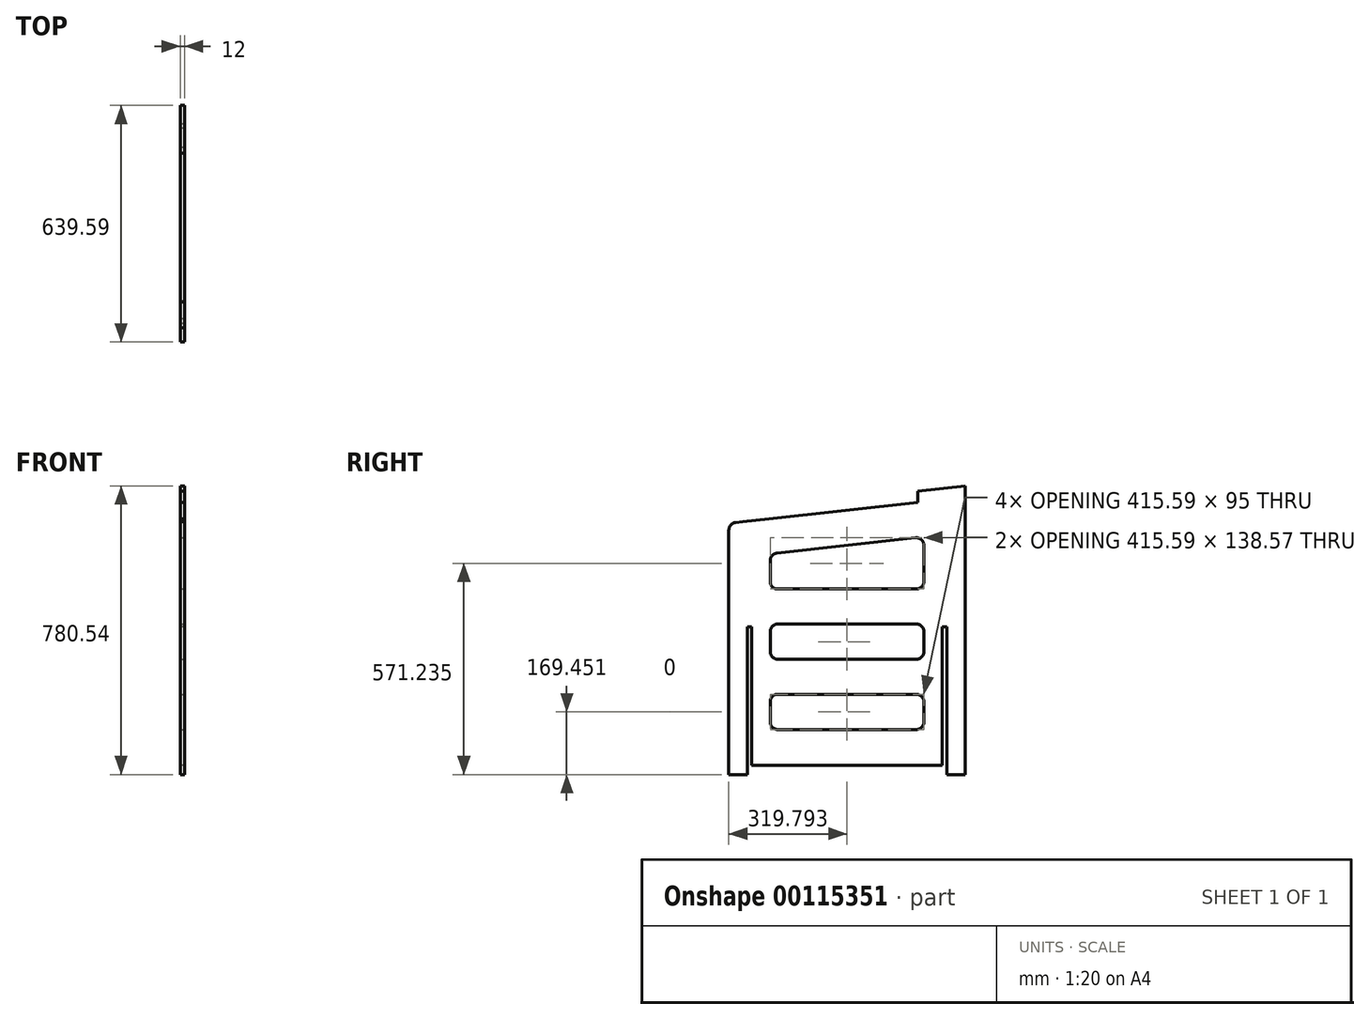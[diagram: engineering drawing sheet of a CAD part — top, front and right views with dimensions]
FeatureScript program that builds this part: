
annotation { "Feature Type Name" : "Feature", "Feature Type Description" : "" }
export const myFeature = defineFeature(function(context is Context, id is Id, definition is map)
    precondition{}
    {
        {
            var Q0;
            Q0=qCreatedBy(makeId("Right.planeOp"),FACE);
            var sketch = newSketch(context, id + "F0", { "sketchPlane" : qUnion([Q0])});
            skLineSegment(sketch, "E0.bottom", {"start": v(-516.8, 134.02) * mm, "end": v(183.2, 127.7) * mm, "construction": true});
            skLineSegment(sketch, "E0.left", {"start": v(-516.8, 134.02) * mm, "end": v(-516.8, 50.2) * mm, "construction": true});
            skLineSegment(sketch, "E1", {"start": v(60.78, -259.53) * mm, "end": v(72.78, -259.53) * mm});
            skLineSegment(sketch, "E2", {"start": v(-466.8, -259.53) * mm, "end": v(-454.8, -259.53) * mm});
            skLineSegment(sketch, "E3", {"start": v(-454.8, -634.53) * mm, "end": v(60.78, -634.53) * mm});
            skLineSegment(sketch, "E4", {"start": v(-478.83, 54.41) * mm, "end": v(-478.83, 24.23) * mm});
            skLineSegment(sketch, "E5", {"start": v(-478.83, 24.23) * mm, "end": v(-498.92, 22.1) * mm});
            skLineSegment(sketch, "E6", {"start": v(-516.8, 2.21) * mm, "end": v(-516.8, -659.53) * mm});
            skLineSegment(sketch, "E7", {"start": v(-516.8, 50.2) * mm, "end": v(-516.8, 20.2) * mm, "construction": true});
            skLineSegment(sketch, "E8", {"start": v(-408.83, 31.98) * mm, "end": v(-5.76, 76.6) * mm});
            skLineSegment(sketch, "E9", {"start": v(-408.83, 62.16) * mm, "end": v(-408.83, 31.98) * mm});
            skLineSegment(sketch, "E10", {"start": v(-516.8, -659.53) * mm, "end": v(-466.8, -659.53) * mm});
            skLineSegment(sketch, "E11", {"start": v(-466.8, -259.53) * mm, "end": v(-466.8, -659.53) * mm});
            skLineSegment(sketch, "E12", {"start": v(-454.8, -259.53) * mm, "end": v(-454.8, -634.53) * mm});
            skLineSegment(sketch, "E13", {"start": v(60.78, -259.53) * mm, "end": v(60.78, -634.53) * mm});
            skLineSegment(sketch, "E14", {"start": v(72.78, -259.53) * mm, "end": v(72.78, -659.53) * mm});
            skLineSegment(sketch, "E15", {"start": v(-516.8, 50.2) * mm, "end": v(-478.83, 54.41) * mm, "construction": true});
            skLineSegment(sketch, "E16", {"start": v(-5.76, 76.6) * mm, "end": v(-5.76, 106.78) * mm});
            skLineSegment(sketch, "E17", {"start": v(-478.83, 54.41) * mm, "end": v(-408.83, 62.16) * mm});
            skLineSegment(sketch, "E18", {"start": v(-408.83, 62.16) * mm, "end": v(-5.76, 106.78) * mm, "construction": true});
            skLineSegment(sketch, "E19", {"start": v(-5.76, 106.78) * mm, "end": v(122.78, 121) * mm});
            skLineSegment(sketch, "E20", {"start": v(122.78, 121) * mm, "end": v(183.2, 127.7) * mm, "construction": true});
            skLineSegment(sketch, "E21", {"start": v(122.78, 121) * mm, "end": v(122.78, -659.53) * mm});
            skLineSegment(sketch, "E22", {"start": v(72.78, -259.53) * mm, "end": v(72.78, 115.47) * mm, "construction": true});
            skLineSegment(sketch, "E23", {"start": v(72.78, -659.53) * mm, "end": v(122.78, -659.53) * mm});
            skLineSegment(sketch, "E24", {"start": v(183.2, 127.7) * mm, "end": v(183.2, -659.53) * mm, "construction": true});
            skLineSegment(sketch, "E25", {"start": v(122.78, -659.53) * mm, "end": v(183.2, -659.53) * mm, "construction": true});
            skPoint(sketch, "E26.visualSharp", {"position": v(-516.8, 20.2) * mm});
            skArc(sketch, "E26.filletArc", {"start": v(-498.92, 22.1) * mm, "mid": v(-511.68, 15.59) * mm, "end": v(-516.8, 2.21) * mm});
            skSolve(sketch);
        }
        {
            var Q0;
            Q0=makeQuery(id+"F0.imprint","IMPRINT",FACE,{"disambiguationData":[TD([[makeQuery(id+"F0.imprint","IMPRINT",EDGE,{"derivedFrom":sQuery(id+"F0.wireOp",EDGE,"E1")}),1.0]])]});
            extrude(context, id + "F1", {"entities" : qUnion([Q0]), "depth" : 12 * mm});
        }
        {
            var Q0;
            Q0=makeQuery(id+"F1.opExtrude","CAP_FACE",FACE,{"disambiguationData":[OSD([sQuery(id+"F0.wireOp",EDGE,"E1"),sQuery(id+"F0.wireOp",EDGE,"E2"),sQuery(id+"F0.wireOp",EDGE,"E3"),sQuery(id+"F0.wireOp",EDGE,"E4"),sQuery(id+"F0.wireOp",EDGE,"E5"),sQuery(id+"F0.wireOp",EDGE,"E6"),sQuery(id+"F0.wireOp",EDGE,"E8"),sQuery(id+"F0.wireOp",EDGE,"E9"),sQuery(id+"F0.wireOp",EDGE,"E10"),sQuery(id+"F0.wireOp",EDGE,"E11"),sQuery(id+"F0.wireOp",EDGE,"E12"),sQuery(id+"F0.wireOp",EDGE,"E13"),sQuery(id+"F0.wireOp",EDGE,"E14"),sQuery(id+"F0.wireOp",EDGE,"E16"),sQuery(id+"F0.wireOp",EDGE,"E17"),sQuery(id+"F0.wireOp",EDGE,"E19"),sQuery(id+"F0.wireOp",EDGE,"E21"),sQuery(id+"F0.wireOp",EDGE,"E23"),sQuery(id+"F0.wireOp",EDGE,"E26.filletArc")])],"isStart":false});
            var sketch = newSketch(context, id + "F2", { "sketchPlane" : qUnion([Q0])});
            skLineSegment(sketch, "E27.left", {"start": v(-404.8, -462.58) * mm, "end": v(-404.8, -517.58) * mm});
            skLineSegment(sketch, "E28.left", {"start": v(-404.8, -272.58) * mm, "end": v(-404.8, -327.58) * mm});
            skLineSegment(sketch, "E29.left", {"start": v(-404.8, -80.49) * mm, "end": v(-404.8, -137.58) * mm});
            skPoint(sketch, "E30", {"position": v(-404.8, -634.53) * mm});
            skPoint(sketch, "E31", {"position": v(-404.8, 32.42) * mm});
            skLineSegment(sketch, "E32", {"start": v(-387.01, -60.6) * mm, "end": v(-11.42, -19.03) * mm});
            skLineSegment(sketch, "E33", {"start": v(10.78, -38.91) * mm, "end": v(10.78, -137.58) * mm});
            skLineSegment(sketch, "E34", {"start": v(-9.22, -157.58) * mm, "end": v(-384.8, -157.58) * mm});
            skLineSegment(sketch, "E35", {"start": v(-384.8, -252.58) * mm, "end": v(-9.22, -252.58) * mm});
            skLineSegment(sketch, "E36", {"start": v(10.78, -272.58) * mm, "end": v(10.78, -327.58) * mm});
            skLineSegment(sketch, "E37", {"start": v(-9.22, -347.58) * mm, "end": v(-384.8, -347.58) * mm});
            skLineSegment(sketch, "E38", {"start": v(-384.8, -442.58) * mm, "end": v(-9.22, -442.58) * mm});
            skLineSegment(sketch, "E39", {"start": v(10.78, -462.58) * mm, "end": v(10.78, -517.58) * mm});
            skLineSegment(sketch, "E40", {"start": v(-9.22, -537.58) * mm, "end": v(-384.8, -537.58) * mm});
            skPoint(sketch, "E41.visualSharp", {"position": v(-404.8, -62.58) * mm});
            skArc(sketch, "E41.filletArc", {"start": v(-387.01, -60.6) * mm, "mid": v(-399.7, -67.15) * mm, "end": v(-404.8, -80.49) * mm});
            skPoint(sketch, "E42.visualSharp", {"position": v(-404.8, -157.58) * mm});
            skArc(sketch, "E42.filletArc", {"start": v(-404.8, -137.58) * mm, "mid": v(-398.95, -151.72) * mm, "end": v(-384.8, -157.58) * mm});
            skPoint(sketch, "E43.visualSharp", {"position": v(10.78, -157.58) * mm});
            skLineSegment(sketch, "E43.filletArc", {"start": v(10.78, -157.58) * mm, "end": v(10.78, -157.58) * mm});
            skPoint(sketch, "E44.visualSharp", {"position": v(10.78, -16.58) * mm});
            skArc(sketch, "E44.filletArc", {"start": v(10.78, -38.91) * mm, "mid": v(4.12, -24.01) * mm, "end": v(-11.42, -19.03) * mm});
            skPoint(sketch, "E45.visualSharp", {"position": v(10.78, -252.58) * mm});
            skArc(sketch, "E45.filletArc", {"start": v(10.78, -272.58) * mm, "mid": v(4.92, -258.44) * mm, "end": v(-9.22, -252.58) * mm});
            skPoint(sketch, "E46.visualSharp", {"position": v(10.78, -347.58) * mm});
            skArc(sketch, "E46.filletArc", {"start": v(-9.22, -347.58) * mm, "mid": v(4.92, -341.72) * mm, "end": v(10.78, -327.58) * mm});
            skPoint(sketch, "E47.visualSharp", {"position": v(-404.8, -347.58) * mm});
            skArc(sketch, "E47.filletArc", {"start": v(-404.8, -327.58) * mm, "mid": v(-398.95, -341.72) * mm, "end": v(-384.8, -347.58) * mm});
            skPoint(sketch, "E48.visualSharp", {"position": v(-404.8, -252.58) * mm});
            skArc(sketch, "E48.filletArc", {"start": v(-384.8, -252.58) * mm, "mid": v(-398.95, -258.44) * mm, "end": v(-404.8, -272.58) * mm});
            skPoint(sketch, "E49.visualSharp", {"position": v(-404.8, -442.58) * mm});
            skArc(sketch, "E49.filletArc", {"start": v(-384.8, -442.58) * mm, "mid": v(-398.95, -448.44) * mm, "end": v(-404.8, -462.58) * mm});
            skPoint(sketch, "E50.visualSharp", {"position": v(10.78, -442.58) * mm});
            skArc(sketch, "E50.filletArc", {"start": v(10.78, -462.58) * mm, "mid": v(4.92, -448.44) * mm, "end": v(-9.22, -442.58) * mm});
            skPoint(sketch, "E51.visualSharp", {"position": v(-404.8, -537.58) * mm});
            skArc(sketch, "E51.filletArc", {"start": v(-404.8, -517.58) * mm, "mid": v(-398.95, -531.72) * mm, "end": v(-384.8, -537.58) * mm});
            skPoint(sketch, "E52.visualSharp", {"position": v(10.78, -537.58) * mm});
            skArc(sketch, "E52.filletArc", {"start": v(-9.22, -537.58) * mm, "mid": v(4.92, -531.72) * mm, "end": v(10.78, -517.58) * mm});
            skArc(sketch, "E53.filletArc", {"start": v(-9.22, -157.58) * mm, "mid": v(4.92, -151.72) * mm, "end": v(10.78, -137.58) * mm});
            skSolve(sketch);
        }
        {
            var Q0;
            Q0=makeQuery(id+"F2.imprint","IMPRINT",FACE,{"disambiguationData":[TD([[makeQuery(id+"F2.imprint","IMPRINT",EDGE,{"derivedFrom":sQuery(id+"F2.wireOp",EDGE,"E29.left")}),1.0]])]});
            var Q1;
            Q1=makeQuery(id+"F2.imprint","IMPRINT",FACE,{"disambiguationData":[TD([[makeQuery(id+"F2.imprint","IMPRINT",EDGE,{"derivedFrom":sQuery(id+"F2.wireOp",EDGE,"E28.left")}),1.0]])]});
            var Q2;
            Q2=makeQuery(id+"F2.imprint","IMPRINT",FACE,{"disambiguationData":[TD([[makeQuery(id+"F2.imprint","IMPRINT",EDGE,{"derivedFrom":sQuery(id+"F2.wireOp",EDGE,"E27.left")}),1.0]])]});
            extrude(context, id + "F3", {"entities" : qUnion([Q0, Q1, Q2]), "operationType" : NewBodyOperationType.REMOVE, "endBound" : BoundingType.THROUGH_ALL, "oppositeDirection" : true, "depth" : 25 * mm});
        }
        {
            var Q0;
            Q0=makeQuery(id+"F1.opExtrude","CAP_FACE",FACE,{"disambiguationData":[OSD([sQuery(id+"F0.wireOp",EDGE,"E1"),sQuery(id+"F0.wireOp",EDGE,"E2"),sQuery(id+"F0.wireOp",EDGE,"E3"),sQuery(id+"F0.wireOp",EDGE,"E4"),sQuery(id+"F0.wireOp",EDGE,"E5"),sQuery(id+"F0.wireOp",EDGE,"E6"),sQuery(id+"F0.wireOp",EDGE,"E8"),sQuery(id+"F0.wireOp",EDGE,"E9"),sQuery(id+"F0.wireOp",EDGE,"E10"),sQuery(id+"F0.wireOp",EDGE,"E11"),sQuery(id+"F0.wireOp",EDGE,"E12"),sQuery(id+"F0.wireOp",EDGE,"E13"),sQuery(id+"F0.wireOp",EDGE,"E14"),sQuery(id+"F0.wireOp",EDGE,"E16"),sQuery(id+"F0.wireOp",EDGE,"E17"),sQuery(id+"F0.wireOp",EDGE,"E19"),sQuery(id+"F0.wireOp",EDGE,"E21"),sQuery(id+"F0.wireOp",EDGE,"E23"),sQuery(id+"F0.wireOp",EDGE,"E26.filletArc")])],"isStart":false});
            var sketch = newSketch(context, id + "F4", { "sketchPlane" : qUnion([Q0])});
            skLineSegment(sketch, "E54", {"start": v(-498.92, 22.1) * mm, "end": v(-345.66, 38.97) * mm});
            skSolve(sketch);
        }
        {
            var Q0;
            {var subQ5=makeQuery(id+"F1.opExtrude","CAP_EDGE",EDGE,{"disambiguationData":[OSD([sQuery(id+"F0.wireOp",EDGE,"E17")])],"isStart":false});Q0=makeQuery(id+"F4.imprint","IMPRINT",FACE,{"disambiguationData":[TD([[makeQuery(id+"F4.imprint","IMPRINT",EDGE,{"derivedFrom":subQ5}),-1.0]])]});}
            extrude(context, id + "F5", {"entities" : qUnion([Q0]), "operationType" : NewBodyOperationType.REMOVE, "endBound" : BoundingType.THROUGH_ALL, "oppositeDirection" : true, "depth" : 25 * mm});
        }
        {
            var Q0;
            Q0=makeQuery(id+"F1.opExtrude","SWEPT_BODY",BODY,{"disambiguationData":[OSD([sQuery(id+"F0.wireOp",EDGE,"E1"),sQuery(id+"F0.wireOp",EDGE,"E2"),sQuery(id+"F0.wireOp",EDGE,"E3"),sQuery(id+"F0.wireOp",EDGE,"E4"),sQuery(id+"F0.wireOp",EDGE,"E5"),sQuery(id+"F0.wireOp",EDGE,"E6"),sQuery(id+"F0.wireOp",EDGE,"E8"),sQuery(id+"F0.wireOp",EDGE,"E9"),sQuery(id+"F0.wireOp",EDGE,"E10"),sQuery(id+"F0.wireOp",EDGE,"E11"),sQuery(id+"F0.wireOp",EDGE,"E12"),sQuery(id+"F0.wireOp",EDGE,"E13"),sQuery(id+"F0.wireOp",EDGE,"E14"),sQuery(id+"F0.wireOp",EDGE,"E16"),sQuery(id+"F0.wireOp",EDGE,"E17"),sQuery(id+"F0.wireOp",EDGE,"E19"),sQuery(id+"F0.wireOp",EDGE,"E21"),sQuery(id+"F0.wireOp",EDGE,"E23"),sQuery(id+"F0.wireOp",EDGE,"E26.filletArc")])]});
            transform(context, id + "F6", {"entities" : qUnion([Q0]), "transformType" : TransformType.TRANSLATION_3D, "dx" : 0 * mm, "dy" : 0 * mm, "dz" : 0 * mm, "makeCopy" : true});
        }
    });
